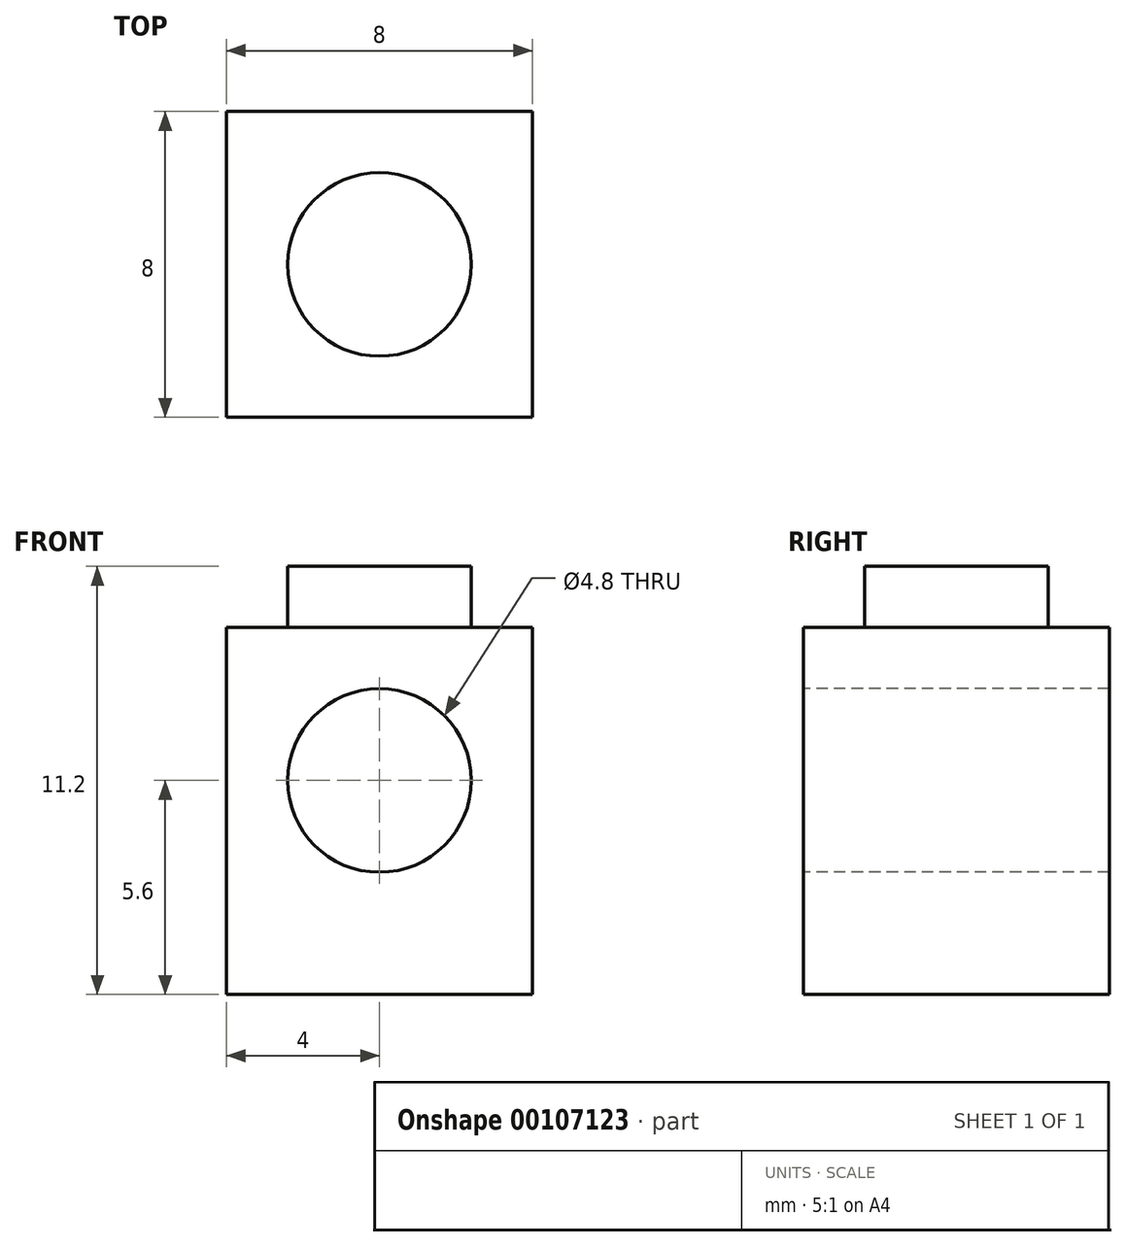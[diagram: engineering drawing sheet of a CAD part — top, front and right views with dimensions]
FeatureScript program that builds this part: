
annotation { "Feature Type Name" : "Feature", "Feature Type Description" : "" }
export const myFeature = defineFeature(function(context is Context, id is Id, definition is map)
    precondition{}
    {
        {
            var Q0;
            Q0=qCreatedBy(makeId("Top.planeOp"),FACE);
            var sketch = newSketch(context, id + "F0", { "sketchPlane" : qUnion([Q0])});
            skLineSegment(sketch, "E0.bottom", {"start": v(0, 0) * mm, "end": v(-8, 0) * mm});
            skLineSegment(sketch, "E0.top", {"start": v(0, 8) * mm, "end": v(-8, 8) * mm});
            skLineSegment(sketch, "E0.left", {"start": v(0, 0) * mm, "end": v(0, 8) * mm});
            skLineSegment(sketch, "E0.right", {"start": v(-8, 0) * mm, "end": v(-8, 8) * mm});
            skSolve(sketch);
        }
        {
            var Q0;
            Q0=makeQuery(id+"F0.imprint","IMPRINT",FACE,{"disambiguationData":[TD([[makeQuery(id+"F0.imprint","IMPRINT",EDGE,{"derivedFrom":sQuery(id+"F0.wireOp",EDGE,"E0.bottom")}),-1.0]])]});
            extrude(context, id + "F1", {"entities" : qUnion([Q0]), "depth" : 9.6 * mm});
        }
        {
            var Q0;
            Q0=makeQuery(id+"F1.opExtrude","SWEPT_FACE",FACE,{"disambiguationData":[OSD([sQuery(id+"F0.wireOp",EDGE,"E0.bottom")])]});
            var sketch = newSketch(context, id + "F2", { "sketchPlane" : qUnion([Q0])});
            skLineSegment(sketch, "E1", {"start": v(-4, 0) * mm, "end": v(-4, 5.6) * mm, "construction": true});
            skCircle(sketch, "E2", {"center": v(-4, 5.6) * mm, "radius": 2.4 * mm});
            skSolve(sketch);
        }
        {
            var Q0;
            Q0=makeQuery(id+"F2.imprint","IMPRINT",FACE,{"disambiguationData":[TD([[makeQuery(id+"F2.imprint","IMPRINT",EDGE,{"derivedFrom":sQuery(id+"F2.wireOp",EDGE,"E2")}),1.0]])]});
            extrude(context, id + "F3", {"entities" : qUnion([Q0]), "operationType" : NewBodyOperationType.REMOVE, "oppositeDirection" : true, "depth" : 25 * mm});
        }
        {
            var Q0;
            Q0=makeQuery(id+"F1.opExtrude","CAP_FACE",FACE,{"disambiguationData":[OSD([sQuery(id+"F0.wireOp",EDGE,"E0.bottom"),sQuery(id+"F0.wireOp",EDGE,"E0.top"),sQuery(id+"F0.wireOp",EDGE,"E0.left"),sQuery(id+"F0.wireOp",EDGE,"E0.right")])],"isStart":false});
            var sketch = newSketch(context, id + "F4", { "sketchPlane" : qUnion([Q0])});
            skCircle(sketch, "E3", {"center": v(-4, 4) * mm, "radius": 2.4 * mm});
            skSolve(sketch);
        }
        {
            var Q0;
            Q0=makeQuery(id+"F4.imprint","IMPRINT",FACE,{"disambiguationData":[TD([[makeQuery(id+"F4.imprint","IMPRINT",EDGE,{"derivedFrom":sQuery(id+"F4.wireOp",EDGE,"E3")}),1.0]])]});
            var Q1;
            Q1=sQuery(id+"F4.wireOp",EDGE,"E3");
            extrude(context, id + "F5", {"entities" : qUnion([Q0]), "operationType" : NewBodyOperationType.ADD, "surfaceEntities" : qUnion([Q1]), "depth" : 1.6 * mm});
        }
    });
